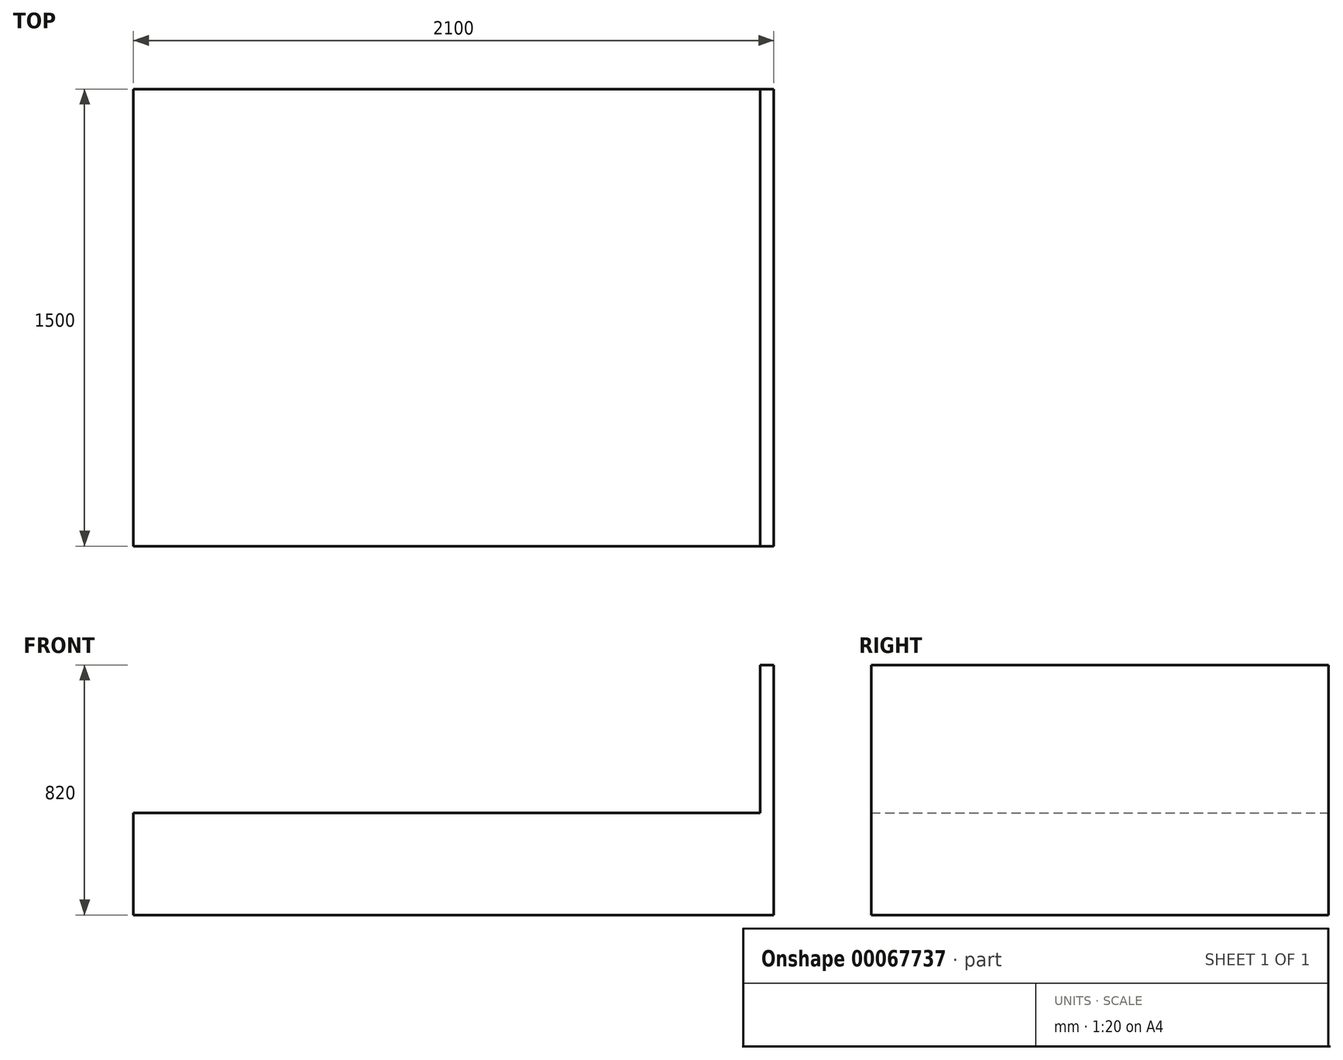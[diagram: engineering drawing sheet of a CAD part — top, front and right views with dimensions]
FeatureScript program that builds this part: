
annotation { "Feature Type Name" : "Feature", "Feature Type Description" : "" }
export const myFeature = defineFeature(function(context is Context, id is Id, definition is map)
    precondition{}
    {
        {
            var Q0;
            Q0=qCreatedBy(makeId("Front.planeOp"),FACE);
            var sketch = newSketch(context, id + "F0", { "sketchPlane" : qUnion([Q0])});
            skLineSegment(sketch, "E0", {"start": v(0, 0) * mm, "end": v(2100, 0) * mm});
            skLineSegment(sketch, "E1", {"start": v(2100, 0) * mm, "end": v(2100, 820) * mm});
            skLineSegment(sketch, "E2", {"start": v(2100, 820) * mm, "end": v(2056, 820) * mm});
            skLineSegment(sketch, "E3", {"start": v(2056, 820) * mm, "end": v(2056, 335.37) * mm});
            skLineSegment(sketch, "E4", {"start": v(2056, 335.37) * mm, "end": v(0, 335.37) * mm});
            skLineSegment(sketch, "E5", {"start": v(0, 335.37) * mm, "end": v(0, 0) * mm});
            skSolve(sketch);
        }
        {
            var Q0;
            Q0=makeQuery(id+"F0.imprint","IMPRINT",FACE,{"disambiguationData":[TD([[makeQuery(id+"F0.imprint","IMPRINT",EDGE,{"derivedFrom":sQuery(id+"F0.wireOp",EDGE,"E0")}),1.0]])]});
            extrude(context, id + "F1", {"entities" : qUnion([Q0]), "depth" : 1500 * mm});
        }
    });
